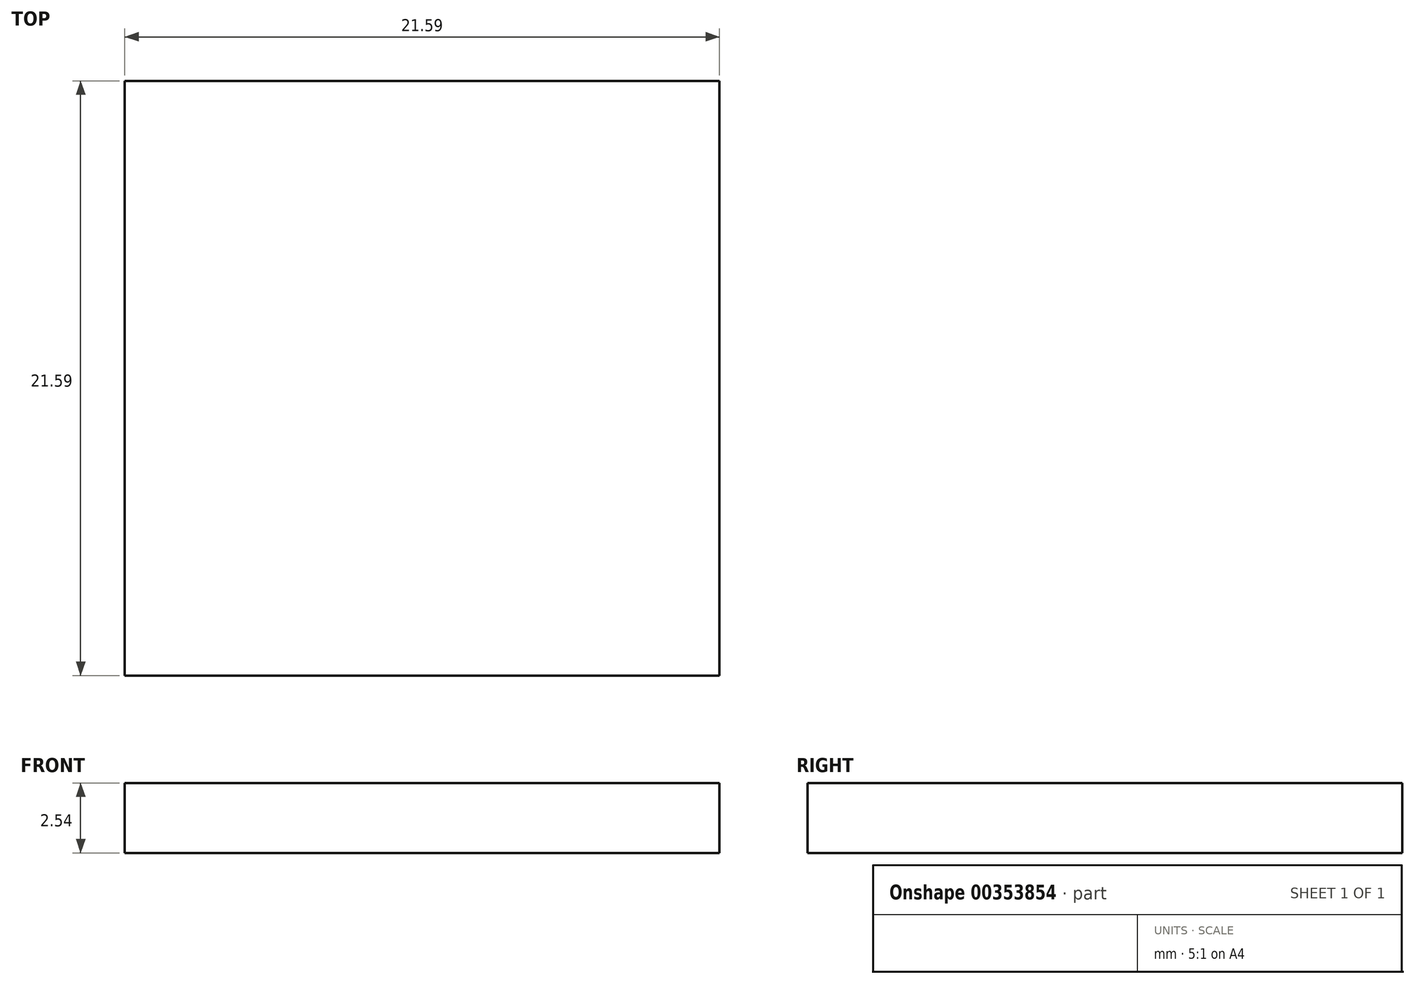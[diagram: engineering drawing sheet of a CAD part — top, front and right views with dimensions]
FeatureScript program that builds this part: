
annotation { "Feature Type Name" : "Feature", "Feature Type Description" : "" }
export const myFeature = defineFeature(function(context is Context, id is Id, definition is map)
    precondition{}
    {
        {
            var Q0;
            Q0=qCreatedBy(makeId("Top.planeOp"),FACE);
            var sketch = newSketch(context, id + "F0", { "sketchPlane" : qUnion([Q0])});
            skLineSegment(sketch, "E0.bottom", {"start": v(0, 0) * mm, "end": v(21.59, 0) * mm});
            skLineSegment(sketch, "E0.top", {"start": v(0, -21.59) * mm, "end": v(21.59, -21.59) * mm});
            skLineSegment(sketch, "E0.left", {"start": v(0, 0) * mm, "end": v(0, -21.59) * mm});
            skLineSegment(sketch, "E0.right", {"start": v(21.59, 0) * mm, "end": v(21.59, -21.59) * mm});
            skSolve(sketch);
        }
        {
            var Q0;
            Q0=makeQuery(id+"F0.imprint","IMPRINT",FACE,{"disambiguationData":[TD([[makeQuery(id+"F0.imprint","IMPRINT",EDGE,{"derivedFrom":sQuery(id+"F0.wireOp",EDGE,"E0.bottom")}),-1.0]])]});
            extrude(context, id + "F1", {"entities" : qUnion([Q0]), "depth" : 2.54 * mm});
        }
    });
